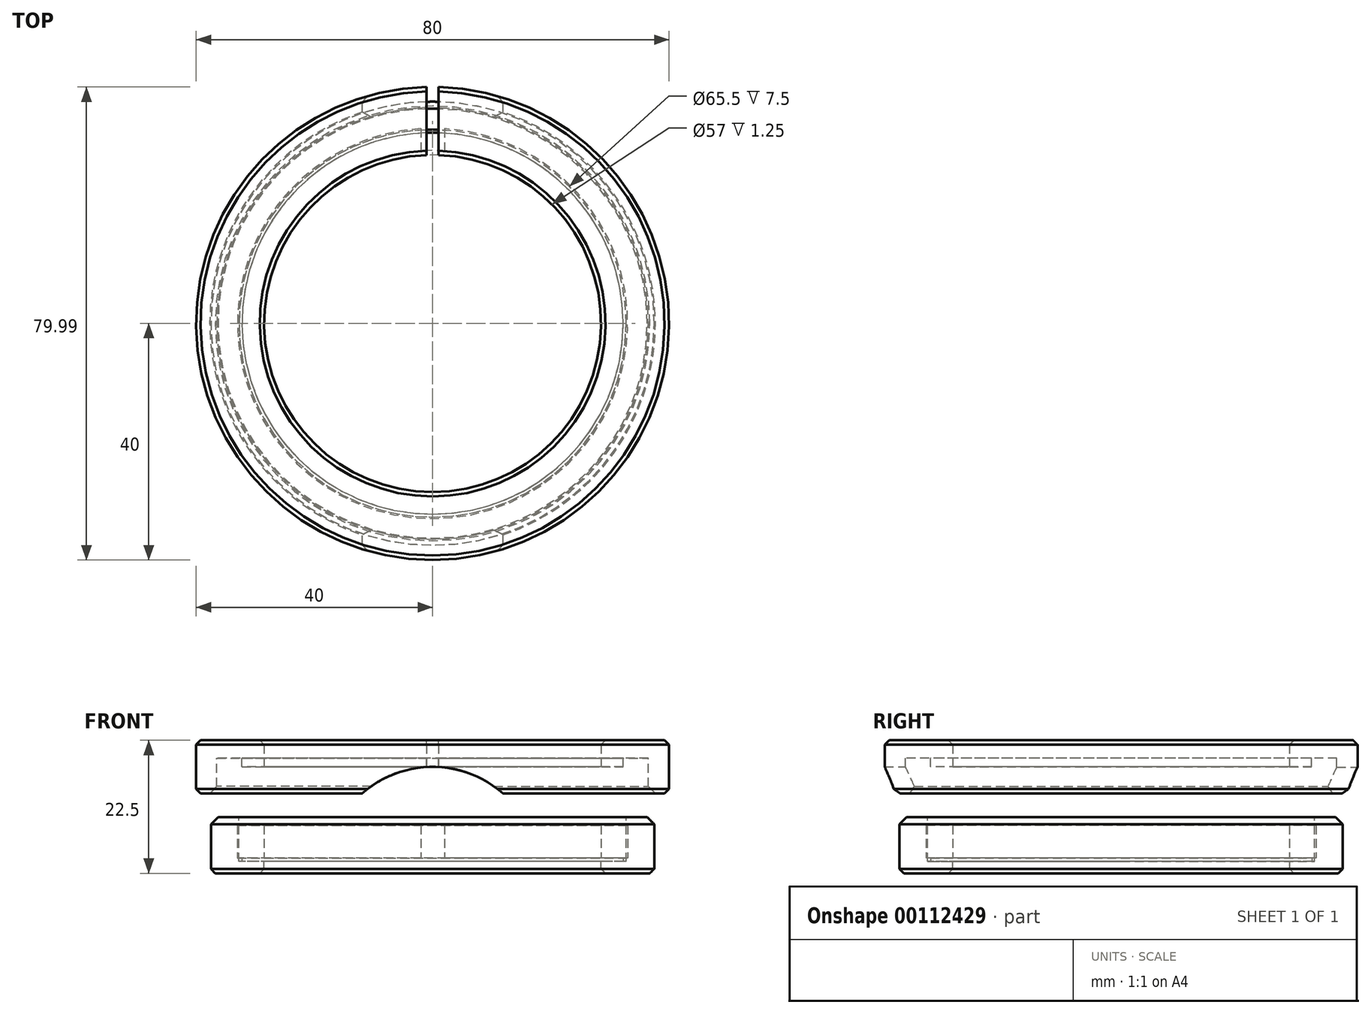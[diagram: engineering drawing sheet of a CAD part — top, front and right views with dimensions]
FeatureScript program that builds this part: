
annotation { "Feature Type Name" : "Feature", "Feature Type Description" : "" }
export const myFeature = defineFeature(function(context is Context, id is Id, definition is map)
    precondition{}
    {
        {
            var Q0;
            Q0=qCreatedBy(makeId("Top.planeOp"),FACE);
            var sketch = newSketch(context, id + "F0", { "sketchPlane" : qUnion([Q0])});
            skCircle(sketch, "E0", {"center": v(0, 0) * mm, "radius": 37.5 * mm});
            skSolve(sketch);
        }
        {
            var Q0;
            Q0=makeQuery(id+"F0.imprint","IMPRINT",FACE,{"disambiguationData":[TD([[makeQuery(id+"F0.imprint","IMPRINT",EDGE,{"derivedFrom":sQuery(id+"F0.wireOp",EDGE,"E0")}),1.0]])]});
            extrude(context, id + "F1", {"entities" : qUnion([Q0]), "depth" : 9.5 * mm});
        }
        {
            var Q0;
            Q0=makeQuery(id+"F1.opExtrude","CAP_FACE",FACE,{"disambiguationData":[OSD([sQuery(id+"F0.wireOp",EDGE,"E0")])],"isStart":false});
            var sketch = newSketch(context, id + "F2", { "sketchPlane" : qUnion([Q0])});
            skCircle(sketch, "E1", {"center": v(0, 0) * mm, "radius": 32.75 * mm});
            skSolve(sketch);
        }
        {
            var Q0;
            Q0=qSketchRegion(id+"F2",true);
            extrude(context, id + "F3", {"entities" : qUnion([Q0]), "operationType" : NewBodyOperationType.REMOVE, "oppositeDirection" : true, "depth" : 7.5 * mm});
        }
        {
            var Q0;
            Q0=makeQuery(id+"F3.boolean.opBoolean","COPY",FACE,{"derivedFrom":makeQuery(id+"F3.opExtrude","CAP_FACE",FACE,{"disambiguationData":[OSD([sQuery(id+"F2.wireOp",EDGE,"E1")])],"isStart":false})});
            var sketch = newSketch(context, id + "F4", { "sketchPlane" : qUnion([Q0])});
            skCircle(sketch, "E2", {"center": v(0, 0) * mm, "radius": 28.5 * mm});
            skSolve(sketch);
        }
        {
            var Q0;
            Q0=qSketchRegion(id+"F4",true);
            extrude(context, id + "F5", {"entities" : qUnion([Q0]), "operationType" : NewBodyOperationType.REMOVE, "oppositeDirection" : true, "depth" : 25 * mm});
        }
        {
            var Q0;
            Q0=makeQuery(id+"F3.boolean.opBoolean","COPY",FACE,{"derivedFrom":makeQuery(id+"F3.opExtrude","CAP_FACE",FACE,{"disambiguationData":[OSD([sQuery(id+"F2.wireOp",EDGE,"E1")])],"isStart":false})});
            var sketch = newSketch(context, id + "F6", { "sketchPlane" : qUnion([Q0])});
            skCircle(sketch, "E3", {"center": v(0, 0) * mm, "radius": 32.25 * mm});
            skSolve(sketch);
        }
        {
            var Q0;
            Q0=qSketchRegion(id+"F6",true);
            extrude(context, id + "F7", {"entities" : qUnion([Q0]), "depth" : .6 * mm});
        }
        {
            var Q0;
            Q0=makeQuery(id+"F7.opExtrude","CAP_FACE",FACE,{"disambiguationData":[OSD([sQuery(id+"F6.wireOp",EDGE,"E3")])],"isStart":false});
            var sketch = newSketch(context, id + "F8", { "sketchPlane" : qUnion([Q0])});
            skArc(sketch, "E4", {"start": v(-2, 32.94) * mm, "mid": v(0, -33) * mm, "end": v(2, 32.94) * mm});
            skArc(sketch, "E5", {"start": v(-2, 28.43) * mm, "mid": v(0, -28.5) * mm, "end": v(2, 28.43) * mm});
            skLineSegment(sketch, "E6.left", {"start": v(-2, 32.94) * mm, "end": v(-2, 28.43) * mm});
            skLineSegment(sketch, "E6.right", {"start": v(2, 32.94) * mm, "end": v(2, 28.43) * mm});
            skSolve(sketch);
        }
        {
            var Q0;
            Q0=qSketchRegion(id+"F8",true);
            extrude(context, id + "F9", {"entities" : qUnion([Q0]), "depth" : 5.5 * mm});
        }
        {
            var Q0;
            Q0=makeQuery(id+"F1.opExtrude","CAP_FACE",FACE,{"disambiguationData":[OSD([sQuery(id+"F0.wireOp",EDGE,"E0")])],"isStart":false});
            cPlane(context, id + "F10", {"entities" : qUnion([Q0]), "cplaneType" : CPlaneType.OFFSET, "offset" : 10 * mm, "width" : 150 * mm, "height" : 150 * mm});
        }
        {
            var Q0;
            Q0=qCreatedBy(id+"F10.planeOp",FACE);
            var sketch = newSketch(context, id + "F11", { "sketchPlane" : qUnion([Q0])});
            skCircle(sketch, "E7", {"center": v(0, 0) * mm, "radius": 40 * mm});
            skCircle(sketch, "E8", {"center": v(0, 0) * mm, "radius": 28.5 * mm});
            skSolve(sketch);
        }
        {
            var Q0;
            Q0 = qSketchRegion(id + "F11", true);
            extrude(context, id + "F12", {"entities" : qUnion([Q0]), "depth" : 3 * mm});
        }
        {
            var Q0;
            Q0=makeQuery(id+"F12.opExtrude","CAP_FACE",FACE,{"disambiguationData":[OSD([sQuery(id+"F11.wireOp",EDGE,"E7"),sQuery(id+"F11.wireOp",EDGE,"E8")])],"isStart":true});
            var sketch = newSketch(context, id + "F13", { "sketchPlane" : qUnion([Q0])});
            skCircle(sketch, "E9", {"center": v(0, 0) * mm, "radius": 40 * mm});
            skCircle(sketch, "E10", {"center": v(0, 0) * mm, "radius": 36.5 * mm});
            skSolve(sketch);
        }
        {
            var Q0;
            Q0 = qSketchRegion(id + "F13", true);
            extrude(context, id + "F14", {"entities" : qUnion([Q0]), "operationType" : NewBodyOperationType.ADD, "depth" : 6 * mm});
        }
        {
            var Q0;
            Q0=makeQuery(id+"F12.opExtrude","CAP_FACE",FACE,{"disambiguationData":[OSD([sQuery(id+"F11.wireOp",EDGE,"E7"),sQuery(id+"F11.wireOp",EDGE,"E8")])],"isStart":true});
            var sketch = newSketch(context, id + "F15", { "sketchPlane" : qUnion([Q0])});
            skCircle(sketch, "E11", {"center": v(0, 0) * mm, "radius": 28.5 * mm});
            skCircle(sketch, "E12", {"center": v(0, 0) * mm, "radius": 32.25 * mm});
            skSolve(sketch);
        }
        {
            var Q0;
            Q0 = qSketchRegion(id + "F15", true);
            extrude(context, id + "F16", {"entities" : qUnion([Q0]), "operationType" : NewBodyOperationType.ADD, "depth" : 1.5 * mm});
        }
        {
            var Q0;
            Q0=makeQuery(id+"F12.opExtrude","CAP_FACE",FACE,{"disambiguationData":[OSD([sQuery(id+"F11.wireOp",EDGE,"E7"),sQuery(id+"F11.wireOp",EDGE,"E8")])],"isStart":false});
            var sketch = newSketch(context, id + "F17", { "sketchPlane" : qUnion([Q0])});
            skLineSegment(sketch, "E13.bottom", {"start": v(-1, 42.3) * mm, "end": v(1, 42.3) * mm});
            skLineSegment(sketch, "E13.top", {"start": v(-1, 25.65) * mm, "end": v(1, 25.65) * mm});
            skLineSegment(sketch, "E13.left", {"start": v(-1, 42.3) * mm, "end": v(-1, 25.65) * mm});
            skLineSegment(sketch, "E13.right", {"start": v(1, 42.3) * mm, "end": v(1, 25.65) * mm});
            skSolve(sketch);
        }
        {
            var Q0;
            Q0 = qSketchRegion(id + "F17", true);
            extrude(context, id + "F18", {"entities" : qUnion([Q0]), "operationType" : NewBodyOperationType.REMOVE, "oppositeDirection" : true, "depth" : 10 * mm});
        }
        {
            var Q0;
            Q0=makeQuery(id+"F1.opExtrude","CAP_EDGE",EDGE,{"disambiguationData":[OSD([sQuery(id+"F0.wireOp",EDGE,"E0")])],"isStart":false});
            var Q1;
            Q1=makeQuery(id+"F14.opExtrude","CAP_EDGE",EDGE,{"disambiguationData":[OSD([sQuery(id+"F13.wireOp",EDGE,"E10")])],"isStart":false});
            chamfer(context, id + "F19", {"entities" : qUnion([Q0, Q1]), "width" : 1.2 * mm, "tangentPropagation" : true});
        }
        {
            var Q0;
            Q0=makeQuery(id+"F1.opExtrude","CAP_EDGE",EDGE,{"disambiguationData":[OSD([sQuery(id+"F0.wireOp",EDGE,"E0")])],"isStart":true});
            var Q1;
            Q1=makeQuery(id+"F12.opExtrude","CAP_EDGE",EDGE,{"disambiguationData":[OSD([sQuery(id+"F11.wireOp",EDGE,"E7")])],"isStart":false});
            var Q2;
            Q2=makeQuery(id+"F12.opExtrude","CAP_EDGE",EDGE,{"disambiguationData":[OSD([sQuery(id+"F11.wireOp",EDGE,"E8")])],"isStart":false});
            var Q3;
            Q3=makeQuery(id+"F14.opExtrude","CAP_EDGE",EDGE,{"disambiguationData":[OSD([sQuery(id+"F13.wireOp",EDGE,"E9")])],"isStart":false});
            var Q4;
            Q4=makeQuery(id+"F5.boolean.opBoolean","INTERSECT",EDGE,{"derivedFrom":[makeQuery(id+"F1.opExtrude","CAP_FACE",FACE,{"disambiguationData":[OSD([sQuery(id+"F0.wireOp",EDGE,"E0")])],"isStart":true}),makeQuery(id+"F5.opExtrude","SWEPT_FACE",FACE,{"disambiguationData":[OSD([sQuery(id+"F4.wireOp",EDGE,"E2")])]})]});
            chamfer(context, id + "F20", {"entities" : qUnion([Q0, Q1, Q2, Q3, Q4]), "width" : .75 * mm, "tangentPropagation" : true});
        }
        {
            var Q0;
            Q0=qCreatedBy(makeId("Front.planeOp"),FACE);
            cPlane(context, id + "F21", {"entities" : qUnion([Q0]), "cplaneType" : CPlaneType.OFFSET, "offset" : 42.9 * mm, "oppositeDirection" : true, "width" : 150 * mm, "height" : 150 * mm});
        }
        {
            var Q0;
            Q0=qCreatedBy(id+"F21.planeOp",FACE);
            var sketch = newSketch(context, id + "F22", { "sketchPlane" : qUnion([Q0])});
            skArc(sketch, "E14", {"start": v(14.04, 11.26) * mm, "mid": v(0, 18) * mm, "end": v(-14.04, 11.26) * mm});
            skLineSegment(sketch, "E15", {"start": v(14.04, 11.26) * mm, "end": v(-14.04, 11.26) * mm});
            skSolve(sketch);
        }
        {
            var Q0;
            Q0 = qSketchRegion(id + "F22", true);
            extrude(context, id + "F23", {"entities" : qUnion([Q0]), "operationType" : NewBodyOperationType.REMOVE, "depth" : 88 * mm});
        }
    });
